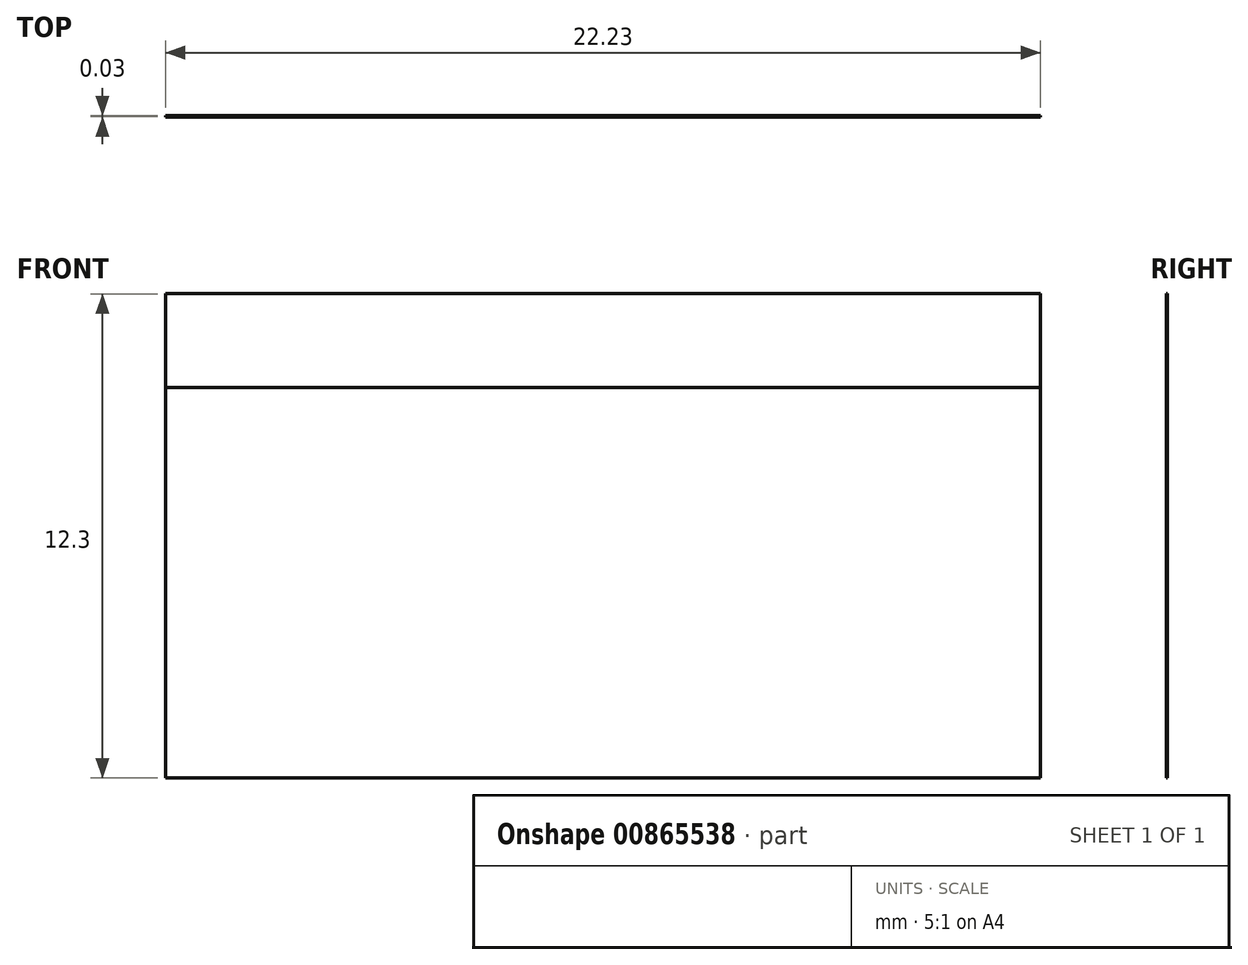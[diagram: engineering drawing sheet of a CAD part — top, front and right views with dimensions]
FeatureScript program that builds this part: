
annotation { "Feature Type Name" : "Feature", "Feature Type Description" : "" }
export const myFeature = defineFeature(function(context is Context, id is Id, definition is map)
    precondition{}
    {
        {
            var Q0;
            Q0=qCreatedBy(makeId("Front.planeOp"),FACE);
            var sketch = newSketch(context, id + "F0", { "sketchPlane" : qUnion([Q0])});
            skLineSegment(sketch, "E0.bottom", {"start": v(0, 0) * mm, "end": v(22.22, 0) * mm});
            skLineSegment(sketch, "E0.top", {"start": v(0, 9.92) * mm, "end": v(22.22, 9.92) * mm});
            skLineSegment(sketch, "E0.left", {"start": v(0, 0) * mm, "end": v(0, 9.92) * mm});
            skLineSegment(sketch, "E0.right", {"start": v(22.22, 0) * mm, "end": v(22.22, 9.92) * mm});
            skSolve(sketch);
        }
        {
            var Q0;
            Q0=makeQuery(id+"F0.imprint","IMPRINT",FACE,{"disambiguationData":[TD([[makeQuery(id+"F0.imprint","IMPRINT",EDGE,{"derivedFrom":sQuery(id+"F0.wireOp",EDGE,"E0.top")}),-1.0]])]});
            extrude(context, id + "F1", {"entities" : qUnion([Q0]), "depth" : 1.75 / 50.8 * mm, "offsetDistance" : 25.4 * mm});
        }
        {
            var Q0;
            Q0=qCreatedBy(makeId("Front.planeOp"),FACE);
            var sketch = newSketch(context, id + "F2", { "sketchPlane" : qUnion([Q0])});
            skLineSegment(sketch, "E1.bottom", {"start": v(0, 9.92) * mm, "end": v(22.23, 9.92) * mm});
            skLineSegment(sketch, "E1.top", {"start": v(0, 12.3) * mm, "end": v(22.23, 12.3) * mm});
            skLineSegment(sketch, "E1.left", {"start": v(0, 9.92) * mm, "end": v(0, 12.3) * mm});
            skLineSegment(sketch, "E1.right", {"start": v(22.23, 9.92) * mm, "end": v(22.23, 12.3) * mm});
            skSolve(sketch);
        }
        {
            var Q0;
            Q0=makeQuery(id+"F2.imprint","IMPRINT",FACE,{"disambiguationData":[TD([[makeQuery(id+"F2.imprint","IMPRINT",EDGE,{"derivedFrom":sQuery(id+"F2.wireOp",EDGE,"E1.bottom")}),1.0]])]});
            var Q1;
            Q1=makeQuery(id+"F2.imprint","IMPRINT",FACE,{"disambiguationData":[TD([[makeQuery(id+"F2.imprint","IMPRINT",EDGE,{"derivedFrom":sQuery(id+"F2.wireOp",EDGE,"582457e2-e852-40e0-b492-1080479f5f9a0.MirrorCS")}),-1.0]])]});
            extrude(context, id + "F3", {"entities" : qUnion([Q0, Q1]), "depth" : 1.75 / 50.8 * mm, "offsetDistance" : 25.4 * mm});
        }
    });
